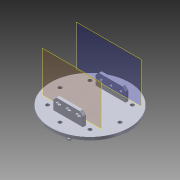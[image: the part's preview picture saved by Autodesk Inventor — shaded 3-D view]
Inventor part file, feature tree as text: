
AUTODESK INVENTOR PART (.ipt)
format: ipt  version: 2013 SP2 (Build 170200200, 200)  size: 304,640 bytes
history: native  units: in
note: dims shown in document units (in); Inventor stores cm internally (conversion verified against a paired STEP export)
features: extrude x6, fillet x6, sketch x6, projected_geometry x4, reference x3, plane x2
ambient origin geometry x8: Origin, YZ Plane, XZ Plane, XY Plane, X Axis, Y Axis, Z Axis, Center Point
bodies: Solid1 (feature_tree)
feature tree (27):
  plane  "Work Plane1"
  extrude  "Extrusion1"  Depth=0.0938in TaperAngle=0.0deg
  fillet  "Fillet1"  Radius=0.01in
  fillet  "Fillet2"  Radius=0.01in
  fillet  "Fillet3"  Radius=0.01in
  fillet  "Fillet4"  Radius=0.01in
  fillet  "Fillet5"  Radius=0.01in
  extrude  "Extrusion2"  Depth=0.0938in TaperAngle=0.0deg
  extrude  "Extrusion3"  Depth=0.118in
  plane  "Work Plane2"
  extrude  "Extrusion4"  Depth=0.118in
  fillet  "Fillet6"  Radius=0.118in
  extrude  "Extrusion5"  Depth=0.118in
  extrude  "Extrusion6"  Depth=4.0in TaperAngle=0.0deg
  sketch  "Sketch1"  dims[d2=0.123in d7=0.0938in d8=0.0in d9=0.01in d10=0.01in d11=0.01in d12=0.01in d13=0.01in]
  reference  "Reference1"
  sketch  "Sketch2"  dims[d14=2.5in d15=0.0938in d16=0.0in]
  reference  "Reference2"
  reference  "Reference3"
  sketch  "Sketch3"  dims[d18=0.118in d21=0.118in]
  projected_geometry  "Projected Loop1"
  sketch  "Sketch4"  dims[d22=0.118in d23=0.118in d24=0.118in]
  projected_geometry  "Projected Loop2"
  sketch  "Sketch5"  dims[d25=0.118in d26=0.118in]
  projected_geometry  "Projected Loop3"
  sketch  "Sketch6"  dims[d27=0.118in d28=4.0in d29=0.0in d30=0.0938in d31=0.0in d32=0.01in d34=0.118in d35=0.228in d36=0.0938in d37=0.0in d38=0.0938in d39=0.0in]
  projected_geometry  "Projected Loop4"
